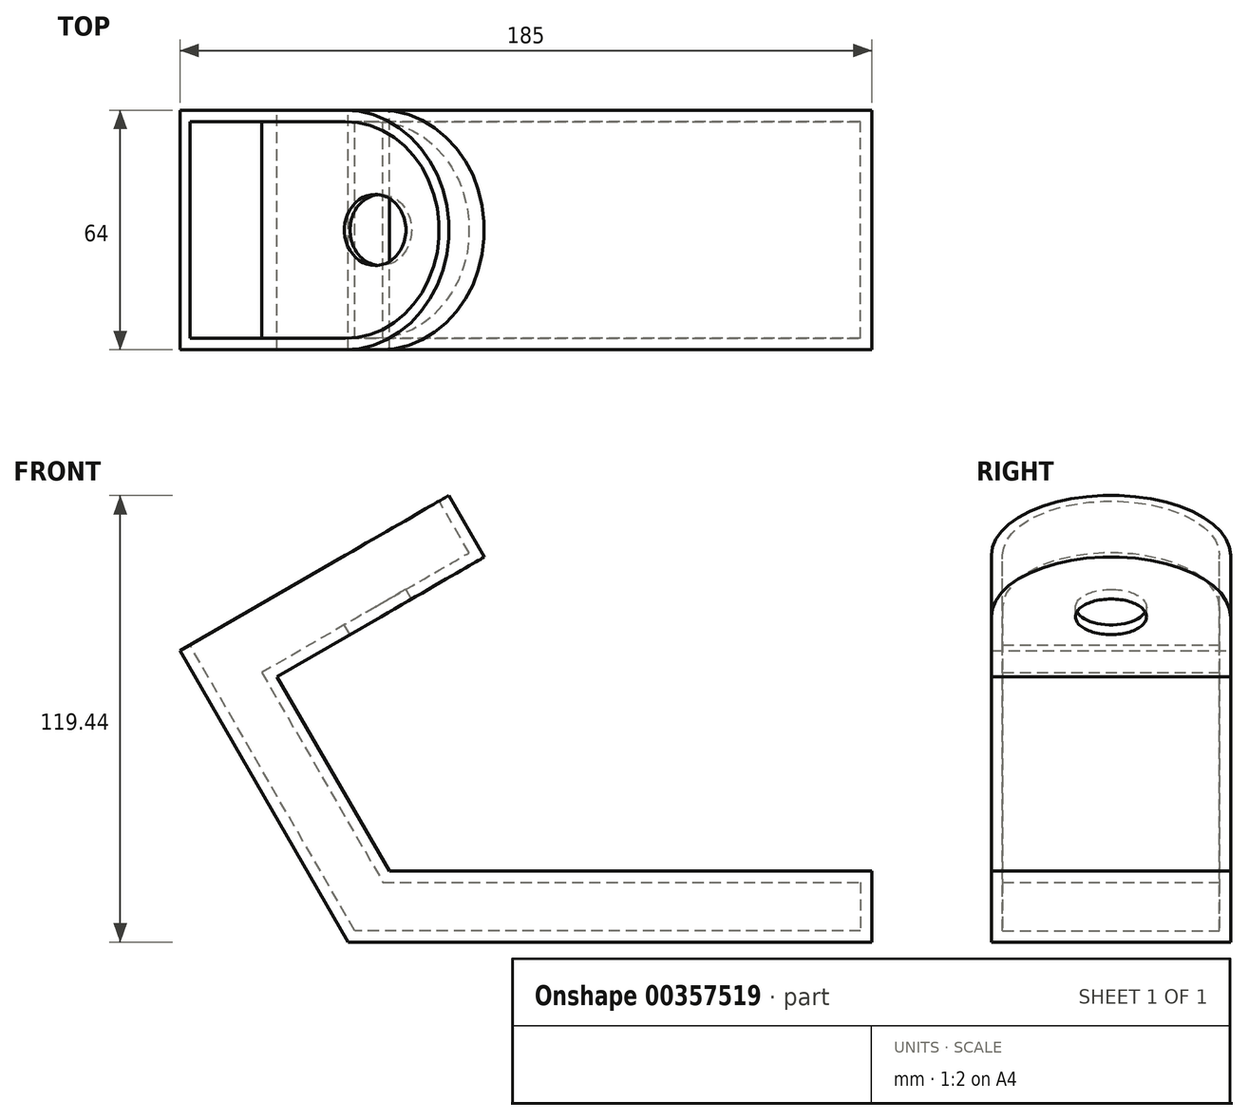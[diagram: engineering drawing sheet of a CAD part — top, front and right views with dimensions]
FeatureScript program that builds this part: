
annotation { "Feature Type Name" : "Feature", "Feature Type Description" : "" }
export const myFeature = defineFeature(function(context is Context, id is Id, definition is map)
    precondition{}
    {
        {
            assignVariable(context, id + "F0", {"name" : "B", "anyValue" : 64 * mm});
        }
        {
            var Q0;
            Q0=qCreatedBy(makeId("Front.planeOp"),FACE);
            var sketch = newSketch(context, id + "F1", { "sketchPlane" : qUnion([Q0])});
            skLineSegment(sketch, "E0", {"start": v(140, 0) * mm, "end": v(0, 0) * mm});
            skLineSegment(sketch, "E1", {"start": v(0, 0) * mm, "end": v(-45, 77.94) * mm});
            skLineSegment(sketch, "E2", {"start": v(-45, 77.94) * mm, "end": v(54.6, 135.44) * mm});
            skLineSegment(sketch, "E3", {"start": v(54.6, 135.44) * mm, "end": v(64.1, 118.99) * mm});
            skLineSegment(sketch, "E4", {"start": v(64.1, 118.99) * mm, "end": v(-19.05, 70.99) * mm});
            skLineSegment(sketch, "E5", {"start": v(10.97, 19) * mm, "end": v(140, 19) * mm});
            skLineSegment(sketch, "E6", {"start": v(140, 19) * mm, "end": v(140, 0) * mm});
            skLineSegment(sketch, "E7", {"start": v(-19.05, 70.99) * mm, "end": v(10.97, 19) * mm});
            skPoint(sketch, "E8", {"position": v(-0.83, 103.44) * mm});
            skSolve(sketch);
        }
        {
            var Q0;
            Q0 = qSketchRegion(id + "F1", true);
            extrude(context, id + "F2", {"entities" : qUnion([Q0]), "depth" : (getVariable(context, 'B'))});
        }
        {
            var Q0;
            Q0=makeQuery(id+"F2.opExtrude","SWEPT_FACE",FACE,{"disambiguationData":[OSD([sQuery(id+"F1.wireOp",EDGE,"E2")])]});
            var sketch = newSketch(context, id + "F3", { "sketchPlane" : qUnion([Q0])});
            skArc(sketch, "E9", {"start": v(51, -64) * mm, "mid": v(83, -32) * mm, "end": v(51, 0) * mm});
            skLineSegment(sketch, "E10", {"start": v(51, 0) * mm, "end": v(51, -64) * mm, "construction": true});
            skSolve(sketch);
        }
        {
            var Q0;
            {var subQ0=sQuery(id+"F3.wireOp",EDGE,"E9");Q0=makeQuery(id+"F3.imprint","IMPRINT",FACE,{"disambiguationData":[TD([[makeQuery(id+"F3.imprint","IMPRINT",EDGE,{"derivedFrom":subQ0}),-1.0]])]});}
            extrude(context, id + "F4", {"entities" : qUnion([Q0]), "operationType" : NewBodyOperationType.REMOVE, "endBound" : BoundingType.UP_TO_NEXT, "oppositeDirection" : true, "depth" : 25.4 * mm});
        }
        {
            var Q0;
            Q0=makeQuery(id+"F2.opExtrude","SWEPT_FACE",FACE,{"disambiguationData":[OSD([sQuery(id+"F1.wireOp",EDGE,"E2")])]});
            shell(context, id + "F5", {"entities" : qUnion([Q0]), "thickness" : 3 * mm});
        }
        {
            var Q0;
            Q0=makeQuery(id+"F5.opShell","OFFSET_FACE",FACE,{"disambiguationData":[OSD([sQuery(id+"F1.wireOp",EDGE,"E4")])]});
            var sketch = newSketch(context, id + "F6", { "sketchPlane" : qUnion([Q0])});
            skCircle(sketch, "E11", {"center": v(51, -32) * mm, "radius": 9.5 * mm});
            skSolve(sketch);
        }
        {
            var Q0;
            Q0 = qSketchRegion(id + "F6", true);
            extrude(context, id + "F7", {"entities" : qUnion([Q0]), "operationType" : NewBodyOperationType.REMOVE, "endBound" : BoundingType.UP_TO_NEXT, "oppositeDirection" : true, "depth" : 25.4 * mm});
        }
    });
